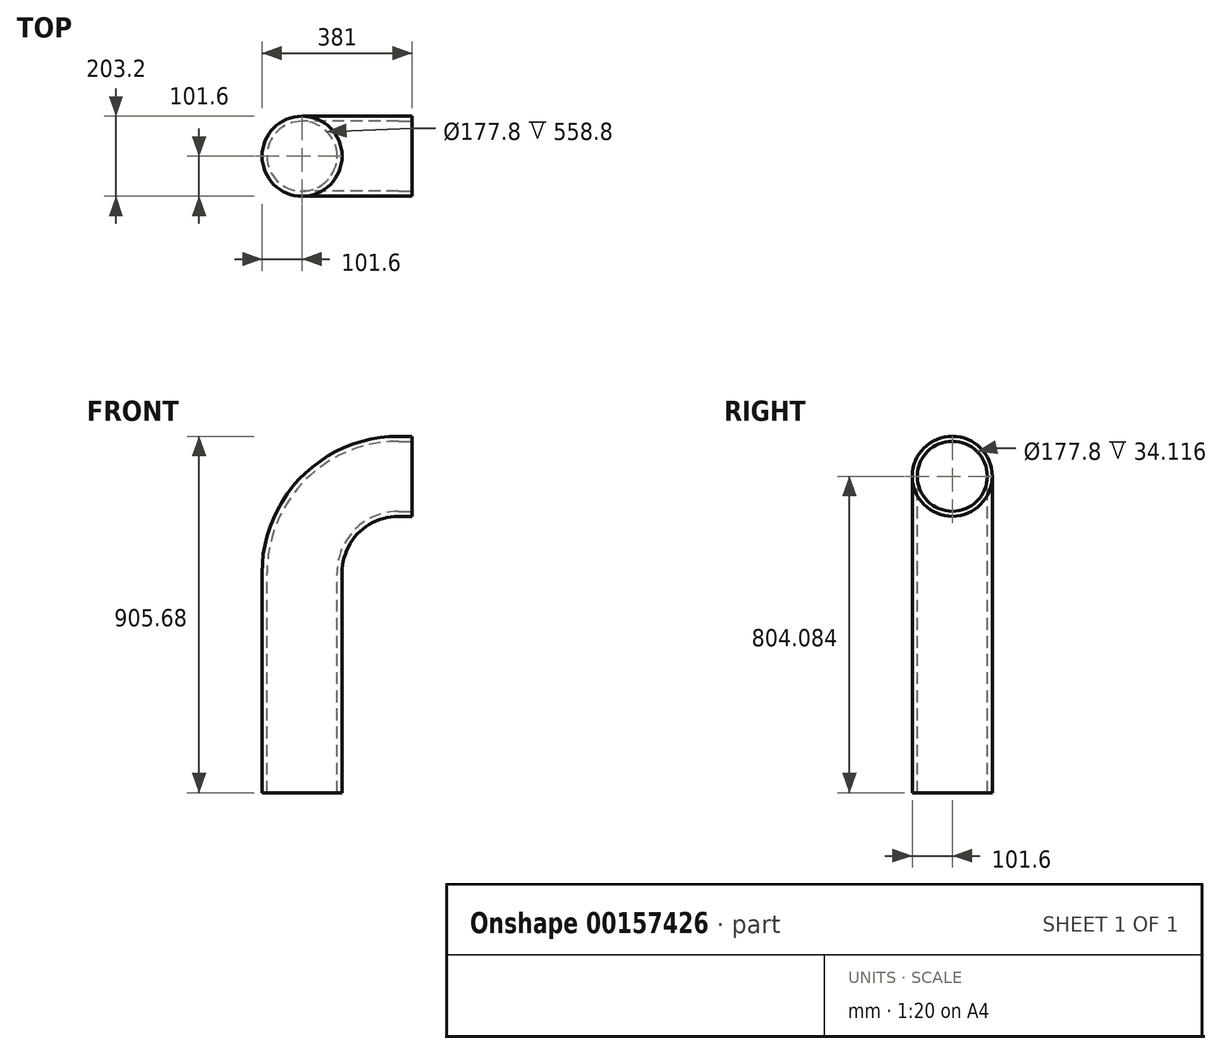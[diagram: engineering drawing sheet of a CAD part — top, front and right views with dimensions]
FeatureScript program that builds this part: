
annotation { "Feature Type Name" : "Feature", "Feature Type Description" : "" }
export const myFeature = defineFeature(function(context is Context, id is Id, definition is map)
    precondition{}
    {
        {
            var Q0;
            Q0=qCreatedBy(makeId("Front.planeOp"),FACE);
            var sketch = newSketch(context, id + "F0", { "sketchPlane" : qUnion([Q0])});
            skLineSegment(sketch, "E0.bottom", {"start": v(0, 0) * mm, "end": v(203.2, 0) * mm});
            skLineSegment(sketch, "E0.left", {"start": v(0, 0) * mm, "end": v(0, 558.8) * mm});
            skLineSegment(sketch, "E0.right", {"start": v(203.2, 0) * mm, "end": v(203.2, 558.8) * mm});
            skLineSegment(sketch, "E1.bottom", {"start": v(346.88, 905.68) * mm, "end": v(609.6, 905.68) * mm});
            skLineSegment(sketch, "E1.right", {"start": v(609.6, 905.68) * mm, "end": v(609.6, 702.48) * mm});
            skArc(sketch, "E2", {"start": v(346.88, 702.48) * mm, "mid": v(245.28, 660.4) * mm, "end": v(203.2, 558.8) * mm});
            skArc(sketch, "E3", {"start": v(346.88, 905.68) * mm, "mid": v(101.6, 804.08) * mm, "end": v(0, 558.8) * mm});
            skLineSegment(sketch, "E4.trimOffspring", {"start": v(346.88, 702.48) * mm, "end": v(609.6, 702.48) * mm});
            skSolve(sketch);
        }
        {
            var Q0;
            Q0=qSketchRegion(id+"F0",true);
            extrude(context, id + "F1", {"entities" : qUnion([Q0]), "depth" : 203.2 * mm});
        }
        {
            var Q0;
            Q0=makeQuery(id+"F1.opExtrude","CAP_EDGE",EDGE,{"disambiguationData":[OSD([sQuery(id+"F0.wireOp",EDGE,"E0.left")])],"isStart":false});
            var Q1;
            Q1=makeQuery(id+"F1.opExtrude","CAP_EDGE",EDGE,{"disambiguationData":[OSD([sQuery(id+"F0.wireOp",EDGE,"E0.right")])],"isStart":false});
            var Q2;
            Q2=makeQuery(id+"F1.opExtrude","CAP_EDGE",EDGE,{"disambiguationData":[OSD([sQuery(id+"F0.wireOp",EDGE,"E0.left")])],"isStart":true});
            var Q3;
            Q3=makeQuery(id+"F1.opExtrude","CAP_EDGE",EDGE,{"disambiguationData":[OSD([sQuery(id+"F0.wireOp",EDGE,"E0.right")])],"isStart":true});
            fillet(context, id + "F2", {"entities" : qUnion([Q0, Q1, Q2, Q3]), "radius" : 101.6 * mm, "tangentPropagation" : true, "allowEdgeOverflow" : false});
        }
        {
            var Q0;
            Q0=makeQuery(id+"F1.opExtrude","SWEPT_FACE",FACE,{"disambiguationData":[OSD([sQuery(id+"F0.wireOp",EDGE,"E0.bottom")])]});
            var Q1;
            Q1=makeQuery(id+"F1.opExtrude","SWEPT_FACE",FACE,{"disambiguationData":[OSD([sQuery(id+"F0.wireOp",EDGE,"E1.right")])]});
            shell(context, id + "F3", {"entities" : qUnion([Q0, Q1]), "thickness" : 12.7 * mm});
        }
        {
            var Q0;
            Q0=makeQuery(id+"F1.opExtrude","SWEPT_FACE",FACE,{"disambiguationData":[OSD([sQuery(id+"F0.wireOp",EDGE,"E1.right")])]});
            extrude(context, id + "F4", {"entities" : qUnion([Q0]), "operationType" : NewBodyOperationType.REMOVE, "oppositeDirection" : true, "depth" : 228.6 * mm});
        }
    });
